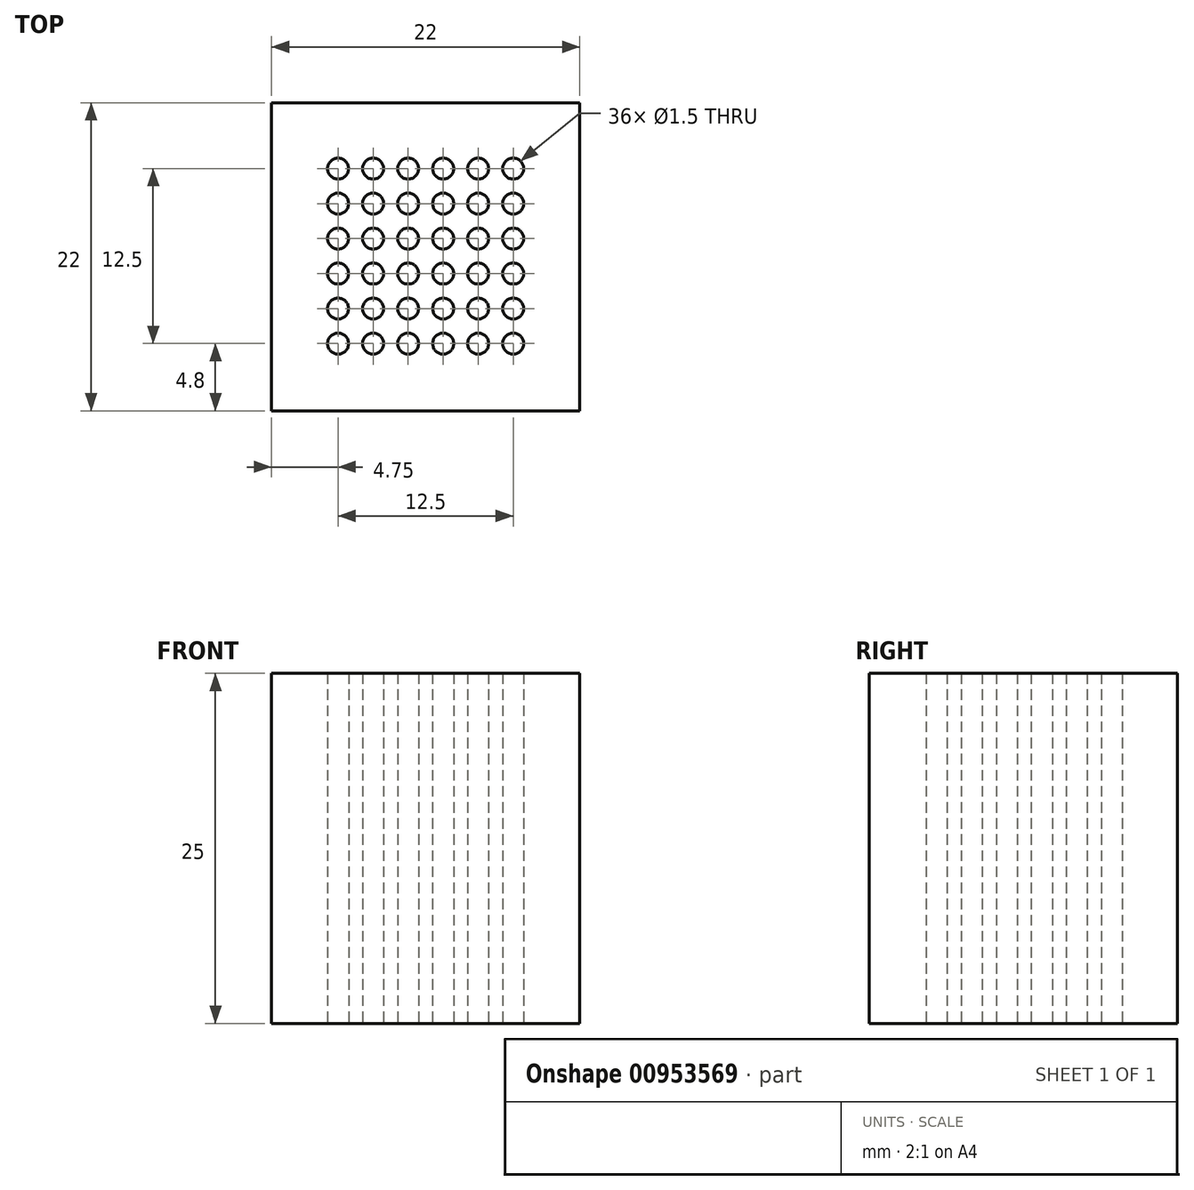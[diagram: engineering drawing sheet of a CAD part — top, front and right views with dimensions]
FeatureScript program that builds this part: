
annotation { "Feature Type Name" : "Feature", "Feature Type Description" : "" }
export const myFeature = defineFeature(function(context is Context, id is Id, definition is map)
    precondition{}
    {
        {
            var Q0;
            Q0=qCreatedBy(makeId("Top.planeOp"),FACE);
            var sketch = newSketch(context, id + "F0", { "sketchPlane" : qUnion([Q0])});
            skLineSegment(sketch, "E0.bottom", {"start": v(-10, 12.25) * mm, "end": v(12, 12.25) * mm});
            skLineSegment(sketch, "E0.top", {"start": v(-10, -9.75) * mm, "end": v(12, -9.75) * mm});
            skLineSegment(sketch, "E0.left", {"start": v(-10, 12.25) * mm, "end": v(-10, -9.75) * mm});
            skLineSegment(sketch, "E0.right", {"start": v(12, 12.25) * mm, "end": v(12, -9.75) * mm});
            skCircle(sketch, "E1", {"center": v(-5.25, 7.55) * mm, "radius": 0.75 * mm});
            skCircle(sketch, "E2.1.0.0", {"center": v(-2.75, 7.55) * mm, "radius": 0.75 * mm});
            skCircle(sketch, "E2.2.0.0", {"center": v(-0.25, 7.55) * mm, "radius": 0.75 * mm});
            skCircle(sketch, "E2.3.0.0", {"center": v(2.25, 7.55) * mm, "radius": 0.75 * mm});
            skCircle(sketch, "E2.4.0.0", {"center": v(4.75, 7.55) * mm, "radius": 0.75 * mm});
            skCircle(sketch, "E2.5.0.0", {"center": v(7.25, 7.55) * mm, "radius": 0.75 * mm});
            skLineSegment(sketch, "E2.direction1", {"start": v(-5.25, 7.55) * mm, "end": v(-2.75, 7.55) * mm, "construction": true});
            skCircle(sketch, "E3.1.0.0", {"center": v(-5.25, 5.05) * mm, "radius": 0.75 * mm});
            skLineSegment(sketch, "E3.1.0.1", {"start": v(-5.25, 5.05) * mm, "end": v(-2.75, 5.05) * mm, "construction": true});
            skCircle(sketch, "E3.1.0.2", {"center": v(4.75, 5.05) * mm, "radius": 0.75 * mm});
            skCircle(sketch, "E3.1.0.3", {"center": v(2.25, 5.05) * mm, "radius": 0.75 * mm});
            skCircle(sketch, "E3.1.0.4", {"center": v(-0.25, 5.05) * mm, "radius": 0.75 * mm});
            skCircle(sketch, "E3.1.0.5", {"center": v(-2.75, 5.05) * mm, "radius": 0.75 * mm});
            skCircle(sketch, "E3.1.0.6", {"center": v(7.25, 5.05) * mm, "radius": 0.75 * mm});
            skCircle(sketch, "E3.2.0.0", {"center": v(-5.25, 2.55) * mm, "radius": 0.75 * mm});
            skLineSegment(sketch, "E3.2.0.1", {"start": v(-5.25, 2.55) * mm, "end": v(-2.75, 2.55) * mm, "construction": true});
            skCircle(sketch, "E3.2.0.2", {"center": v(4.75, 2.55) * mm, "radius": 0.75 * mm});
            skCircle(sketch, "E3.2.0.3", {"center": v(2.25, 2.55) * mm, "radius": 0.75 * mm});
            skCircle(sketch, "E3.2.0.4", {"center": v(-0.25, 2.55) * mm, "radius": 0.75 * mm});
            skCircle(sketch, "E3.2.0.5", {"center": v(-2.75, 2.55) * mm, "radius": 0.75 * mm});
            skCircle(sketch, "E3.2.0.6", {"center": v(7.25, 2.55) * mm, "radius": 0.75 * mm});
            skCircle(sketch, "E3.3.0.0", {"center": v(-5.25, 0.05) * mm, "radius": 0.75 * mm});
            skLineSegment(sketch, "E3.3.0.1", {"start": v(-5.25, 0.05) * mm, "end": v(-2.75, 0.05) * mm, "construction": true});
            skCircle(sketch, "E3.3.0.2", {"center": v(4.75, 0.05) * mm, "radius": 0.75 * mm});
            skCircle(sketch, "E3.3.0.3", {"center": v(2.25, 0.05) * mm, "radius": 0.75 * mm});
            skCircle(sketch, "E3.3.0.4", {"center": v(-0.25, 0.05) * mm, "radius": 0.75 * mm});
            skCircle(sketch, "E3.3.0.5", {"center": v(-2.75, 0.05) * mm, "radius": 0.75 * mm});
            skCircle(sketch, "E3.3.0.6", {"center": v(7.25, 0.05) * mm, "radius": 0.75 * mm});
            skCircle(sketch, "E3.4.0.0", {"center": v(-5.25, -2.45) * mm, "radius": 0.75 * mm});
            skLineSegment(sketch, "E3.4.0.1", {"start": v(-5.25, -2.45) * mm, "end": v(-2.75, -2.45) * mm, "construction": true});
            skCircle(sketch, "E3.4.0.2", {"center": v(4.75, -2.45) * mm, "radius": 0.75 * mm});
            skCircle(sketch, "E3.4.0.3", {"center": v(2.25, -2.45) * mm, "radius": 0.75 * mm});
            skCircle(sketch, "E3.4.0.4", {"center": v(-0.25, -2.45) * mm, "radius": 0.75 * mm});
            skCircle(sketch, "E3.4.0.5", {"center": v(-2.75, -2.45) * mm, "radius": 0.75 * mm});
            skCircle(sketch, "E3.4.0.6", {"center": v(7.25, -2.45) * mm, "radius": 0.75 * mm});
            skCircle(sketch, "E3.5.0.0", {"center": v(-5.25, -4.95) * mm, "radius": 0.75 * mm});
            skLineSegment(sketch, "E3.5.0.1", {"start": v(-5.25, -4.95) * mm, "end": v(-2.75, -4.95) * mm, "construction": true});
            skCircle(sketch, "E3.5.0.2", {"center": v(4.75, -4.95) * mm, "radius": 0.75 * mm});
            skCircle(sketch, "E3.5.0.3", {"center": v(2.25, -4.95) * mm, "radius": 0.75 * mm});
            skCircle(sketch, "E3.5.0.4", {"center": v(-0.25, -4.95) * mm, "radius": 0.75 * mm});
            skCircle(sketch, "E3.5.0.5", {"center": v(-2.75, -4.95) * mm, "radius": 0.75 * mm});
            skCircle(sketch, "E3.5.0.6", {"center": v(7.25, -4.95) * mm, "radius": 0.75 * mm});
            skLineSegment(sketch, "E3.direction1", {"start": v(-5.25, 7.55) * mm, "end": v(-5.25, 5.05) * mm, "construction": true});
            skSolve(sketch);
        }
        {
            var Q0;
            Q0=makeQuery(id+"F0.imprint","IMPRINT",FACE,{"disambiguationData":[TD([[makeQuery(id+"F0.imprint","IMPRINT",EDGE,{"derivedFrom":sQuery(id+"F0.wireOp",EDGE,"E0.bottom")}),-1.0]])]});
            extrude(context, id + "F1", {"entities" : qUnion([Q0]), "depth" : 25 * mm, "offsetDistance" : 25 * mm});
        }
    });
